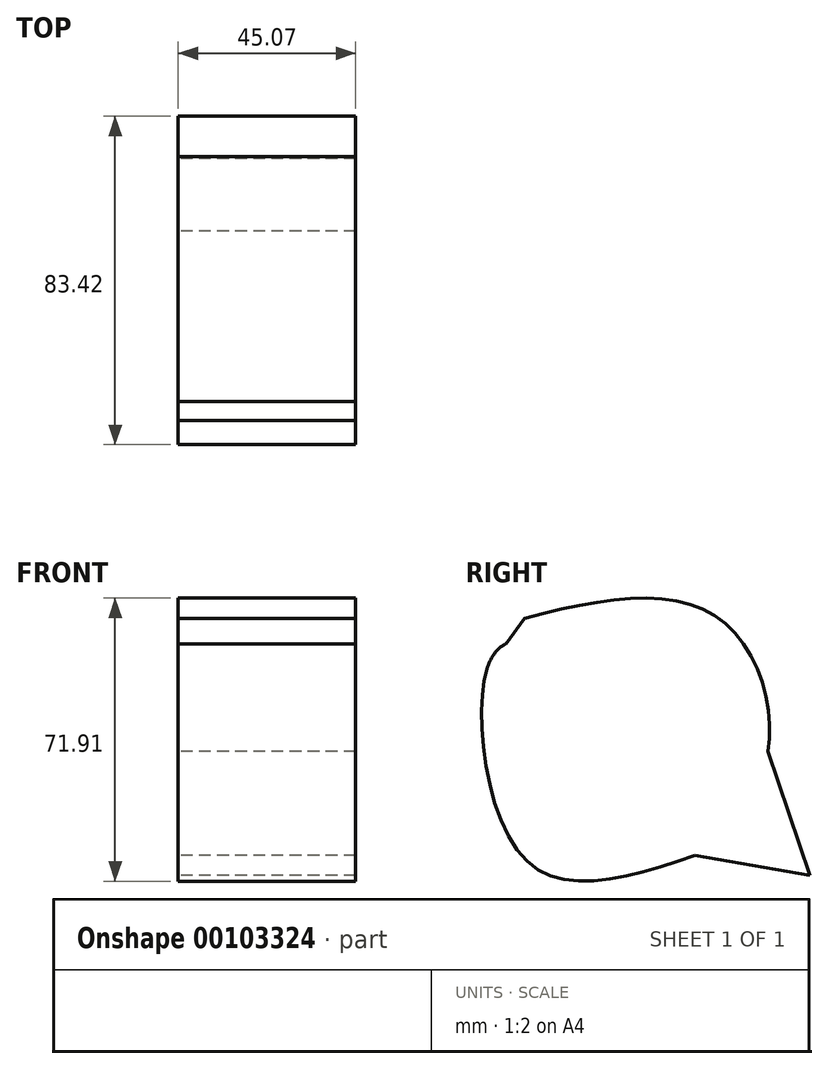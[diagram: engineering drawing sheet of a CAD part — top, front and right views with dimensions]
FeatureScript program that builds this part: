
annotation { "Feature Type Name" : "Feature", "Feature Type Description" : "" }
export const myFeature = defineFeature(function(context is Context, id is Id, definition is map)
    precondition{}
    {
        {
            var Q0;
            Q0=qCreatedBy(makeId("Right.planeOp"),FACE);
            var sketch = newSketch(context, id + "F0", { "sketchPlane" : qUnion([Q0])});
            skLineSegment(sketch, "E0", {"start": v(-64.62, 59.67) * mm, "end": v(-21.8, 60.38) * mm});
            skLineSegment(sketch, "E1", {"start": v(-21.8, 60.38) * mm, "end": v(6.73, 38.7) * mm});
            skLineSegment(sketch, "E2", {"start": v(6.73, 38.7) * mm, "end": v(17.46, 7.2) * mm});
            skLineSegment(sketch, "E3", {"start": v(17.46, 7.2) * mm, "end": v(-11.74, 12.32) * mm});
            skLineSegment(sketch, "E4", {"start": v(-11.74, 12.32) * mm, "end": v(-38.3, 37.52) * mm});
            skLineSegment(sketch, "E5", {"start": v(-38.3, 37.52) * mm, "end": v(-55, 72.5) * mm});
            skLineSegment(sketch, "E6", {"start": v(-64.62, 59.67) * mm, "end": v(-55, 72.5) * mm});
            skFitSpline(sketch, "E7", {"points": [v(-59.8, 66.09) * mm, v(-64.62, 59.67) * mm, v(-54.67, 11.07) * mm, v(-11.74, 12.32) * mm], "startDerivative": vector(-20.43, -10.98) * mm, "endDerivative": vector(122.26, 41.74) * mm});
            skFitSpline(sketch, "E8", {"points": [v(-55, 72.5) * mm, v(-5.67, 72.47) * mm, v(6.73, 38.7) * mm, v(-11.74, 12.32) * mm], "startDerivative": vector(156.42, 42.98) * mm, "endDerivative": vector(-82.46, -77) * mm});
            skSolve(sketch);
        }
        {
            var Q0;
            Q0 = qSketchRegion(id + "F0", true);
            extrude(context, id + "F1", {"entities" : qUnion([Q0]), "depth" : 45.07 * mm});
        }
    });
